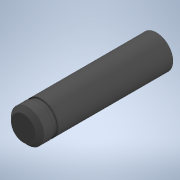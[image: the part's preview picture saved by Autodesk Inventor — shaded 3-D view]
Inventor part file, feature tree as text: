
AUTODESK INVENTOR PART (.ipt)
format: ipt  version: 2022 (Build 260153000, 153)  size: 133,632 bytes
history: native  units: mm
features: extrude x3, sketch x3, chamfer x1
ambient origin geometry x8: Origin, YZ Plane, XZ Plane, XY Plane, X Axis, Y Axis, Z Axis, Center Point
bodies: Solid1 (feature_tree)
feature tree (7):
  extrude  "Extrusion1"  Depth=10.8mm TaperAngle=0.0deg
  extrude  "Extrusion2"  Depth=0.5mm TaperAngle=0.0deg
  extrude  "Extrusion3"  Depth=0.5mm TaperAngle=45.0deg
  chamfer  "Chamfer1"  Distance=3.2mm
  sketch  "Sketch1"  dims[d0=4.0mm d1=10.8mm d2=0.0mm]
  sketch  "Sketch2"  dims[d3=3.8mm d4=0.5mm d5=0.0mm]
  sketch  "Sketch3"  dims[d6=1.65mm d7=0.0mm d8=0.5mm d9=2.0mm d10=45.0deg d11=3.2mm d12=0.0mm]
